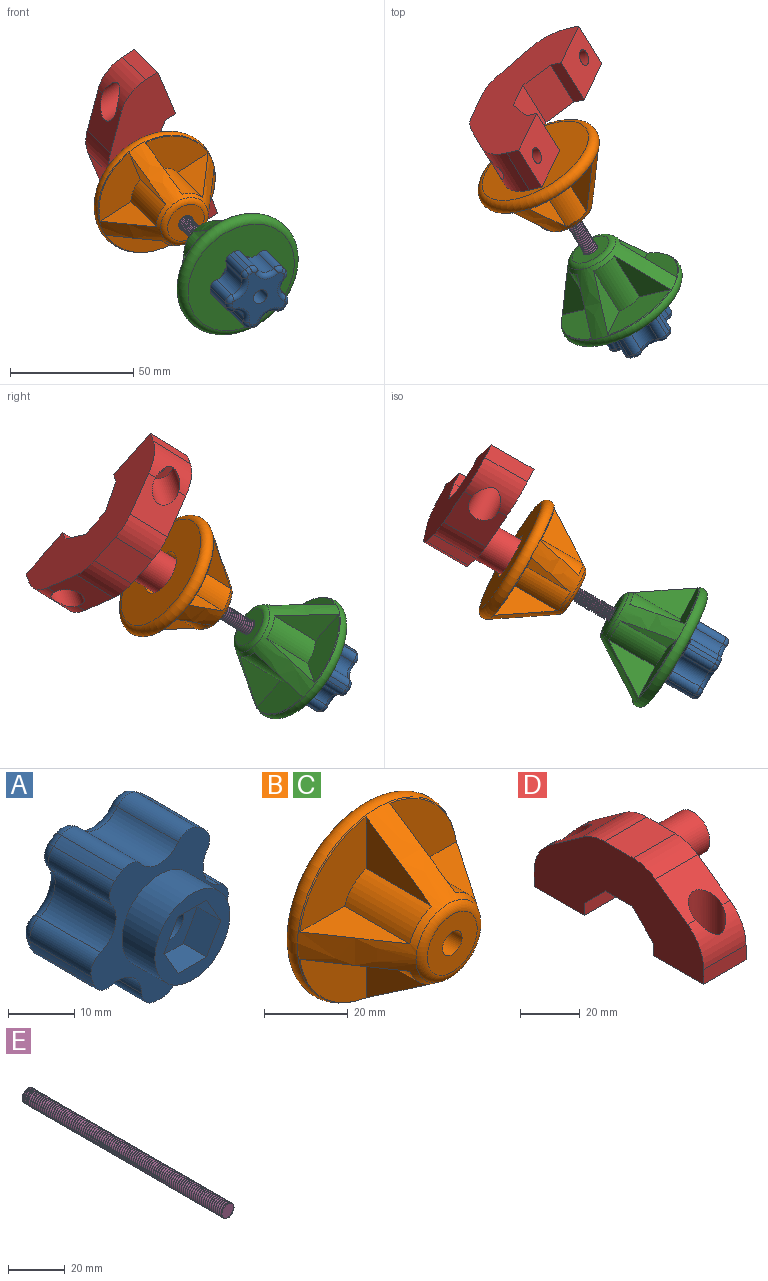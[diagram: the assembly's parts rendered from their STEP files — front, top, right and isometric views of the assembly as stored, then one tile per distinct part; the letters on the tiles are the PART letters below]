
ASSEMBLY  parts=5 mates=4
PART A: 52 faces, bbox 29.3x22x28.2 mm
  f0: plane 16x16mm, normal (0,-1,0), area 105.6mm2, adj f8,f24,f25,f26,f27,f28,f29
  f1: cylinder r=15mm len=13mm, axis (0,1,0), area 26.6mm2, adj f5,f14,f17,f50
  f2: cylinder r=15mm len=13mm, axis (0,1,0), area 26.6mm2, adj f5,f16,f19,f42
  f3: cylinder r=15mm len=13mm, axis (0,1,0), area 26.6mm2, adj f5,f18,f21,f34
  f4: cylinder r=15mm len=13mm, axis (0,1,0), area 26.6mm2, adj f5,f20,f23,f37
  f5: plane 29.28x28.17mm, normal (0,-1,0), area 305.3mm2, adj f1,f2,f3,f4,f7,f8,f9,f10
  f6: plane 25.28x24.17mm, normal (0,1,0), area 286.1mm2, adj f31,f32,f33,f34,f35,f36,f37,f38
  f7: cylinder r=15mm len=13mm, axis (0,1,0), area 26.6mm2, adj f5,f15,f22,f45
  f8: cylinder r=8mm len=16mm, axis (0,1,0), area 351.9mm2, adj f0,f5
  f9: cylinder r=5mm len=13mm, axis (0,1,0), area 119.9mm2, adj f5,f22,f23,f41
  f10: cylinder r=5mm len=13mm, axis (0,1,0), area 119.9mm2, adj f5,f20,f21,f33
  f11: cylinder r=5mm len=13mm, axis (0,1,0), area 119.9mm2, adj f5,f18,f19,f38
  f12: cylinder r=5mm len=13mm, axis (0,1,0), area 119.9mm2, adj f5,f16,f17,f46
  f13: cylinder r=5mm len=13mm, axis (0,1,0), area 119.9mm2, adj f5,f14,f15,f49
  f14: cylinder r=3mm len=13mm, axis (0,-1,0), area 57.8mm2, adj f1,f5,f13,f51
  f15: cylinder r=3mm len=13mm, axis (0,1,0), area 57.8mm2, adj f5,f7,f13,f47
  f16: cylinder r=3mm len=13mm, axis (0,-1,0), area 57.8mm2, adj f2,f5,f12,f44
  f17: cylinder r=3mm len=13mm, axis (0,1,0), area 57.8mm2, adj f1,f5,f12,f48
  f18: cylinder r=3mm len=13mm, axis (0,-1,0), area 57.8mm2, adj f3,f5,f11,f36
  f19: cylinder r=3mm len=13mm, axis (0,1,0), area 57.8mm2, adj f2,f5,f11,f40
  f20: cylinder r=3mm len=13mm, axis (0,-1,0), area 57.8mm2, adj f4,f5,f10,f35
  f21: cylinder r=3mm len=13mm, axis (0,1,0), area 57.8mm2, adj f3,f5,f10,f32
  f22: cylinder r=3mm len=13mm, axis (0,-1,0), area 57.8mm2, adj f5,f7,f9,f43
  f23: cylinder r=3mm len=13mm, axis (0,1,0), area 57.8mm2, adj f4,f5,f9,f39
  f24: plane 5.25x5mm, normal (0.87,0,-0.5), area 30.3mm2, adj f0,f25,f29,f30
  f25: plane 5.25x5mm, normal (0.87,0,0.5), area 30.3mm2, adj f0,f24,f26,f30
  f26: plane 6.06x5mm, normal (0,0,1), area 30.3mm2, adj f0,f25,f27,f30
  f27: plane 5.25x5mm, normal (-0.87,0,0.5), area 30.3mm2, adj f0,f26,f28,f30
  f28: plane 5.25x5mm, normal (-0.87,0,-0.5), area 30.3mm2, adj f0,f27,f29,f30
  f29: plane 6.06x5mm, normal (0,0,-1), area 30.3mm2, adj f0,f24,f28,f30
  f30: plane 12.12x10.5mm, normal (0,-1,0), area 64.3mm2, adj f24,f25,f26,f27,f28,f29,f31
  f31: cylinder r=3.15mm len=17mm, axis (0,-1,0), area 336.5mm2, adj f6,f30
  f32: torus R=1mm, axis (0,1,0), area 10.6mm2, adj f6,f21,f33,f34
  f33: torus R=7mm, axis (0,1,0), area 33.2mm2, adj f6,f10,f32,f35
  f34: torus R=13mm, axis (0,1,0), area 6.1mm2, adj f3,f6,f32,f36
  f35: torus R=1mm, axis (0,1,0), area 10.6mm2, adj f6,f20,f33,f37
  f36: torus R=1mm, axis (0,1,0), area 10.6mm2, adj f6,f18,f34,f38
  f37: torus R=13mm, axis (0,1,0), area 6.1mm2, adj f4,f6,f35,f39
  f38: torus R=7mm, axis (0,1,0), area 33.2mm2, adj f6,f11,f36,f40
  f39: torus R=1mm, axis (0,1,0), area 10.6mm2, adj f6,f23,f37,f41
  f40: torus R=1mm, axis (0,1,0), area 10.6mm2, adj f6,f19,f38,f42
  f41: torus R=7mm, axis (0,1,0), area 33.2mm2, adj f6,f9,f39,f43
  f42: torus R=13mm, axis (0,1,0), area 6.1mm2, adj f2,f6,f40,f44
  f43: torus R=1mm, axis (0,1,0), area 10.6mm2, adj f6,f22,f41,f45
  f44: torus R=1mm, axis (0,1,0), area 10.6mm2, adj f6,f16,f42,f46
  f45: torus R=13mm, axis (0,1,0), area 6.1mm2, adj f6,f7,f43,f47
  f46: torus R=7mm, axis (0,1,0), area 33.2mm2, adj f6,f12,f44,f48
  f47: torus R=1mm, axis (0,1,0), area 10.6mm2, adj f6,f15,f45,f49
  f48: torus R=1mm, axis (0,1,0), area 10.6mm2, adj f6,f17,f46,f50
  f49: torus R=7mm, axis (0,1,0), area 33.2mm2, adj f6,f13,f47,f51
  f50: torus R=13mm, axis (0,1,0), area 6.1mm2, adj f1,f6,f48,f51
  f51: torus R=1mm, axis (0,1,0), area 10.6mm2, adj f6,f14,f49,f50
PART B: 26 faces, bbox 59.3x30x59.3 mm
  f0: cone r=10mm half-angle=33.7deg, axis (0,1,0), area 1065.1mm2, adj f8,f9,f10,f11,f12,f13,f14,f15
  f1: cylinder r=8.7mm len=17.4mm, axis (0,1,0), area 356.4mm2, adj f5,f6
  f2: cylinder r=3.3mm len=14.76mm, axis (0,-1,0), area 305.9mm2, adj f4,f5
  f3: plane 48.79x48.79mm, normal (0,1,0), area 1586mm2, adj f7,f24
  f4: plane 16.79x16.79mm, normal (0,-1,0), area 187.2mm2, adj f2,f25
  f5: cone r=0mm half-angle=59deg, axis (0,1,0), area 237.5mm2, adj f1,f2
  f6: cone r=0mm half-angle=59deg, axis (0,1,0), area 53.4mm2, adj f1,f7
  f7: cylinder r=9.5mm len=19mm, axis (0,1,0), area 298.5mm2, adj f3,f6
  f8: plane 22x15.05mm, normal (1,0,0), area 166.7mm2, adj f0,f10,f11
  f9: plane 22x15.05mm, normal (0,0,-1), area 166.7mm2, adj f0,f10,f11
  f10: cylinder r=12mm len=22mm, axis (0,-1,0), area 235.3mm2, adj f0,f8,f9,f11
  f11: plane 22.37x22.37mm, normal (0,-1,0), area 327.1mm2, adj f0,f8,f9,f10
  f12: plane 22x15.05mm, normal (1,0,0), area 166.7mm2, adj f0,f13,f15
  f13: cylinder r=12mm len=22mm, axis (0,-1,0), area 235.3mm2, adj f0,f12,f14,f15
  f14: plane 22x15.05mm, normal (0,0,1), area 166.7mm2, adj f0,f13,f15
  f15: plane 22.37x22.37mm, normal (0,-1,0), area 327.1mm2, adj f0,f12,f13,f14
  f16: plane 22x15.05mm, normal (0,0,1), area 166.7mm2, adj f0,f17,f19
  f17: cylinder r=12mm len=22mm, axis (0,-1,0), area 235.3mm2, adj f0,f16,f18,f19
  f18: plane 22x15.05mm, normal (-1,0,0), area 166.7mm2, adj f0,f17,f19
  f19: plane 22.37x22.37mm, normal (0,-1,0), area 327.1mm2, adj f0,f16,f17,f18
  f20: plane 22x15.05mm, normal (-1,0,0), area 166.7mm2, adj f0,f21,f23
  f21: cylinder r=12mm len=22mm, axis (0,-1,0), area 235.3mm2, adj f0,f20,f22,f23
  f22: plane 22x15.05mm, normal (0,0,-1), area 166.7mm2, adj f0,f21,f23
  f23: plane 22.37x22.37mm, normal (0,-1,0), area 327.1mm2, adj f0,f20,f21,f22
  f24: torus R=24.39mm, axis (0,-1,0), area 1080.6mm2, adj f0,f3
  f25: torus R=8.39mm, axis (0,1,0), area 180.7mm2, adj f0,f4
PART C: same geometry as B
PART D: 35 faces, bbox 35x80x35 mm
  f0: plane 16x16mm, normal (1,0,0), area 107.4mm2, adj f13,f14,f15,f16,f17,f18,f19
  f1: plane 20x15.29mm, normal (0,-0.58,0.81), area 286.8mm2, adj f11,f12,f26,f29,f32
  f2: plane 20x6.05mm, normal (0,-1,0), area 120.9mm2, adj f3,f11,f12,f29
  f3: plane 23.62x20mm, normal (0,0,-1), area 438.3mm2, adj f2,f4,f11,f12,f27
  f4: plane 20x5mm, normal (0,1,0), area 100mm2, adj f3,f11,f12,f33
  f5: plane 20x12.75mm, normal (0,0,-1), area 255mm2, adj f11,f12,f33,f34
  f6: plane 20x5mm, normal (0,-1,0), area 100mm2, adj f7,f11,f12,f34
  f7: plane 23.62x20mm, normal (0,0,-1), area 438.3mm2, adj f6,f8,f11,f12,f23
  f8: plane 20x6.05mm, normal (0,1,0), area 120.9mm2, adj f7,f11,f12,f30
  f9: plane 20x15.29mm, normal (0,0.58,0.81), area 286.8mm2, adj f11,f12,f25,f30,f31
  f10: plane 20x13.43mm, normal (0,0,1), area 268.6mm2, adj f11,f12,f31,f32
  f11: plane 80x35mm, normal (-1,0,0), area 1834.6mm2, adj f1,f2,f3,f4,f5,f6,f7,f8
  f12: plane 80x35mm, normal (1,0,0), area 1633.5mm2, adj f1,f2,f3,f4,f5,f6,f7,f8
  f13: cylinder r=8mm len=16mm, axis (-1,0,0), area 754mm2, adj f0,f12
  f14: plane 5.18x5mm, normal (0,0.51,-0.86), area 30mm2, adj f0,f15,f19,f20
  f15: plane 6x5mm, normal (0,1,0.01), area 30mm2, adj f0,f14,f16,f20
  f16: plane 5.22x5mm, normal (0,0.49,0.87), area 30mm2, adj f0,f15,f17,f20
  f17: plane 5.18x5mm, normal (0,-0.51,0.86), area 30mm2, adj f0,f16,f18,f20
  f18: plane 6x5mm, normal (0,-1,-0.01), area 30mm2, adj f0,f17,f19,f20
  f19: plane 5.22x5mm, normal (0,-0.49,-0.87), area 30mm2, adj f0,f14,f18,f20
  f20: plane 12.01x10.44mm, normal (1,0,0), area 62.5mm2, adj f14,f15,f16,f17,f18,f19,f22
  f21: cone r=0mm half-angle=59deg, axis (1,0,0), area 36.4mm2, adj f22
  f22: cylinder r=3.15mm len=25mm, axis (1,0,0), area 494.8mm2, adj f20,f21
  f23: cylinder r=3.3mm len=6.6mm, axis (0,0,1), area 100.4mm2, adj f7,f24
  f24: plane 12.5x12.5mm, normal (0,0,1), area 88.5mm2, adj f23,f25
  f25: cylinder r=6.25mm len=20.96mm, axis (0,0,1), area 628.5mm2, adj f9,f24,f30
  f26: cylinder r=6.25mm len=20.96mm, axis (0,0,1), area 628.5mm2, adj f1,f28,f29
  f27: cylinder r=3.3mm len=6.6mm, axis (0,0,1), area 100.4mm2, adj f3,f28
  f28: plane 12.5x12.5mm, normal (0,0,1), area 88.5mm2, adj f26,f27
  f29: cylinder r=18mm len=20mm, axis (-1,0,0), area 268.5mm2, adj f1,f2,f11,f12,f26
  f30: cylinder r=18mm len=20mm, axis (-1,0,0), area 268.5mm2, adj f8,f9,f11,f12,f25
  f31: cylinder r=18mm len=20mm, axis (1,0,0), area 223.9mm2, adj f9,f10,f11,f12
  f32: cylinder r=18mm len=20mm, axis (-1,0,0), area 223.9mm2, adj f1,f10,f11,f12
  f33: plane 20x10mm, normal (0,0.71,-0.71), area 282.8mm2, adj f4,f5,f11,f12
  f34: plane 20x10mm, normal (0,-0.71,-0.71), area 282.8mm2, adj f5,f6,f11,f12
PART E: 7 faces, bbox 6.6x101.2x7.5 mm
  f0: cylinder r=3mm len=100mm, axis (0,-1,0), area -1283.7mm2, adj f1,f2,f3,f4,f5,f6
  f1: plane 6.15x5.92mm, normal (0,1,0), area 22.9mm2, adj f0,f3,f4,f5
  f2: plane 6.07x6.07mm, normal (0,-1,0), area 28mm2, adj f0,f5,f6
  f3: plane 0.22x0.13mm, normal (0,0,1), area 0mm2, adj f0,f1,f5
  f4: bspline ~100.27x6.93mm, area 1426.1mm2, adj f0,f1,f5,f6
  f5: bspline ~100.43x6.93mm, area 1423.8mm2, adj f0,f1,f2,f3,f4,f6
  f6: plane 0.75x0.74mm, normal (0,0,-1), area 0.3mm2, adj f0,f2,f4,f5
PLACE A rot(axis=(-0.95,-0.19,-0.24),144.9deg) t=(-8.13,-42.23,34.74)mm
PLACE B rot(axis=(0.72,-0.54,0.43),49.6deg) t=(-52.36,28.79,78.59)mm
PLACE C rot(axis=(0.23,0.31,-0.92),159deg) t=(-15.94,-29.7,42.48)mm
PLACE D rot(axis=(0.84,-0.34,-0.42),147.4deg) t=(-37.51,43.23,97.19)mm
PLACE E rot(axis=(-0.95,-0.19,-0.24),144.9deg) t=(-42.19,12.59,68.18)mm
MATE slider B.f0 <-> E.f1  axis (-0.47,0.75,0.46) through (-45.23,17.33,71.51)mm
MATE slider A.f1 <-> E.f1  axis (-0.47,0.75,0.46) through (-18.43,-25.69,44.96)mm
MATE fastened E.f0 <-> D.f13  axis (-0.47,0.75,0.46) through (-65.29,49.67,91.07)mm
MATE slider C.f0 <-> E.f1  axis (-0.47,0.75,0.46) through (-29.99,-7.14,56.41)mm
